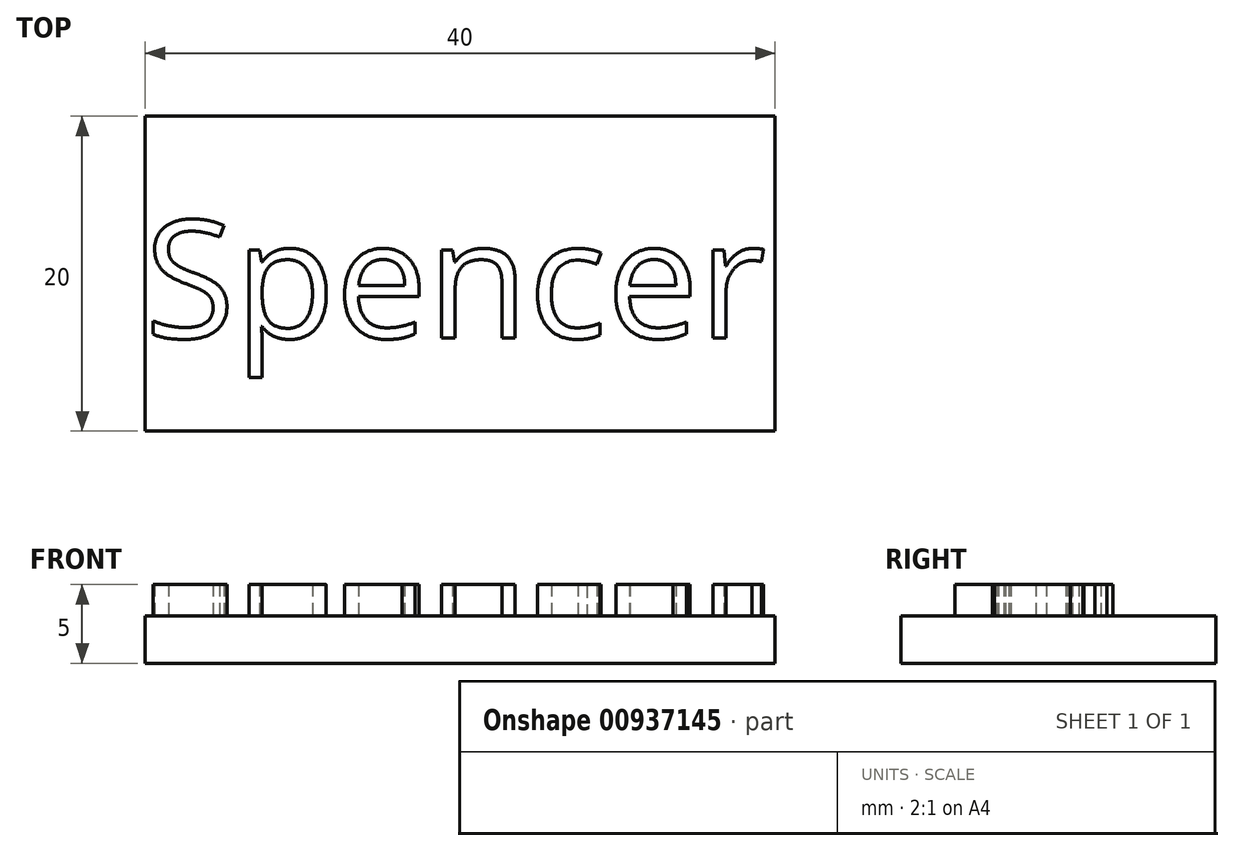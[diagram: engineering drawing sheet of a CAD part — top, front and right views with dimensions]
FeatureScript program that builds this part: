
annotation { "Feature Type Name" : "Feature", "Feature Type Description" : "" }
export const myFeature = defineFeature(function(context is Context, id is Id, definition is map)
    precondition{}
    {
        {
            var Q0;
            Q0=qCreatedBy(makeId("Top.planeOp"),FACE);
            var sketch = newSketch(context, id + "F0", { "sketchPlane" : qUnion([Q0])});
            skLineSegment(sketch, "E0.bottom", {"start": v(3.94, 22.88) * mm, "end": v(43.94, 22.88) * mm});
            skLineSegment(sketch, "E0.top", {"start": v(3.94, 2.88) * mm, "end": v(43.94, 2.88) * mm});
            skLineSegment(sketch, "E0.left", {"start": v(3.94, 22.88) * mm, "end": v(3.94, 2.88) * mm});
            skLineSegment(sketch, "E0.right", {"start": v(43.94, 22.88) * mm, "end": v(43.94, 2.88) * mm});
            skSolve(sketch);
        }
        {
            var Q0;
            Q0=makeQuery(id+"F0.imprint","IMPRINT",FACE,{"disambiguationData":[TD([[makeQuery(id+"F0.imprint","IMPRINT",EDGE,{"derivedFrom":sQuery(id+"F0.wireOp",EDGE,"E0.bottom")}),-1.0]])]});
            extrude(context, id + "F1", {"entities" : qUnion([Q0]), "depth" : 3 * mm, "offsetDistance" : 25 * mm});
        }
        {
            var Q0;
            Q0=qCreatedBy(makeId("Top.planeOp"),FACE);
            var sketch = newSketch(context, id + "F2", { "sketchPlane" : qUnion([Q0])});
            skText(sketch, "E1", { "text": "Spencer", "fontName": "OpenSans-Regular.ttf"});
            const initialGuessF2  = {"E1": [0.0039, 0.0088, 1, 0, 0.00751]};
            skSetInitialGuess(sketch, initialGuessF2);
            skSolve(sketch);
        }
        {
            var Q0;
            Q0=makeQuery(id+"F2.imprint","IMPRINT",FACE,{"disambiguationData":[TD([[makeQuery(id+"F2.imprint","IMPRINT",EDGE,{"derivedFrom":sQuery(id+"F2.wireOp",EDGE,"E1.sketch_text.stroke-0")}),-1.0]])]});
            var Q1;
            Q1=makeQuery(id+"F2.imprint","IMPRINT",FACE,{"disambiguationData":[TD([[makeQuery(id+"F2.imprint","IMPRINT",EDGE,{"derivedFrom":sQuery(id+"F2.wireOp",EDGE,"E1.sketch_text.stroke-25")}),-1.0]])]});
            var Q2;
            Q2=makeQuery(id+"F2.imprint","IMPRINT",FACE,{"disambiguationData":[TD([[makeQuery(id+"F2.imprint","IMPRINT",EDGE,{"derivedFrom":sQuery(id+"F2.wireOp",EDGE,"E1.sketch_text.stroke-50")}),-1.0]])]});
            var Q3;
            Q3=makeQuery(id+"F2.imprint","IMPRINT",FACE,{"disambiguationData":[TD([[makeQuery(id+"F2.imprint","IMPRINT",EDGE,{"derivedFrom":sQuery(id+"F2.wireOp",EDGE,"E1.sketch_text.stroke-69")}),-1.0]])]});
            var Q4;
            Q4=makeQuery(id+"F2.imprint","IMPRINT",FACE,{"disambiguationData":[TD([[makeQuery(id+"F2.imprint","IMPRINT",EDGE,{"derivedFrom":sQuery(id+"F2.wireOp",EDGE,"E1.sketch_text.stroke-86")}),-1.0]])]});
            var Q5;
            Q5=makeQuery(id+"F2.imprint","IMPRINT",FACE,{"disambiguationData":[TD([[makeQuery(id+"F2.imprint","IMPRINT",EDGE,{"derivedFrom":sQuery(id+"F2.wireOp",EDGE,"E1.sketch_text.stroke-101")}),-1.0]])]});
            var Q6;
            Q6=makeQuery(id+"F2.imprint","IMPRINT",FACE,{"disambiguationData":[TD([[makeQuery(id+"F2.imprint","IMPRINT",EDGE,{"derivedFrom":sQuery(id+"F2.wireOp",EDGE,"E1.sketch_text.stroke-120")}),-1.0]])]});
            extrude(context, id + "F3", {"entities" : qUnion([Q0, Q1, Q2, Q3, Q4, Q5, Q6]), "operationType" : NewBodyOperationType.ADD, "depth" : 5 * mm, "offsetDistance" : 25 * mm});
        }
    });
